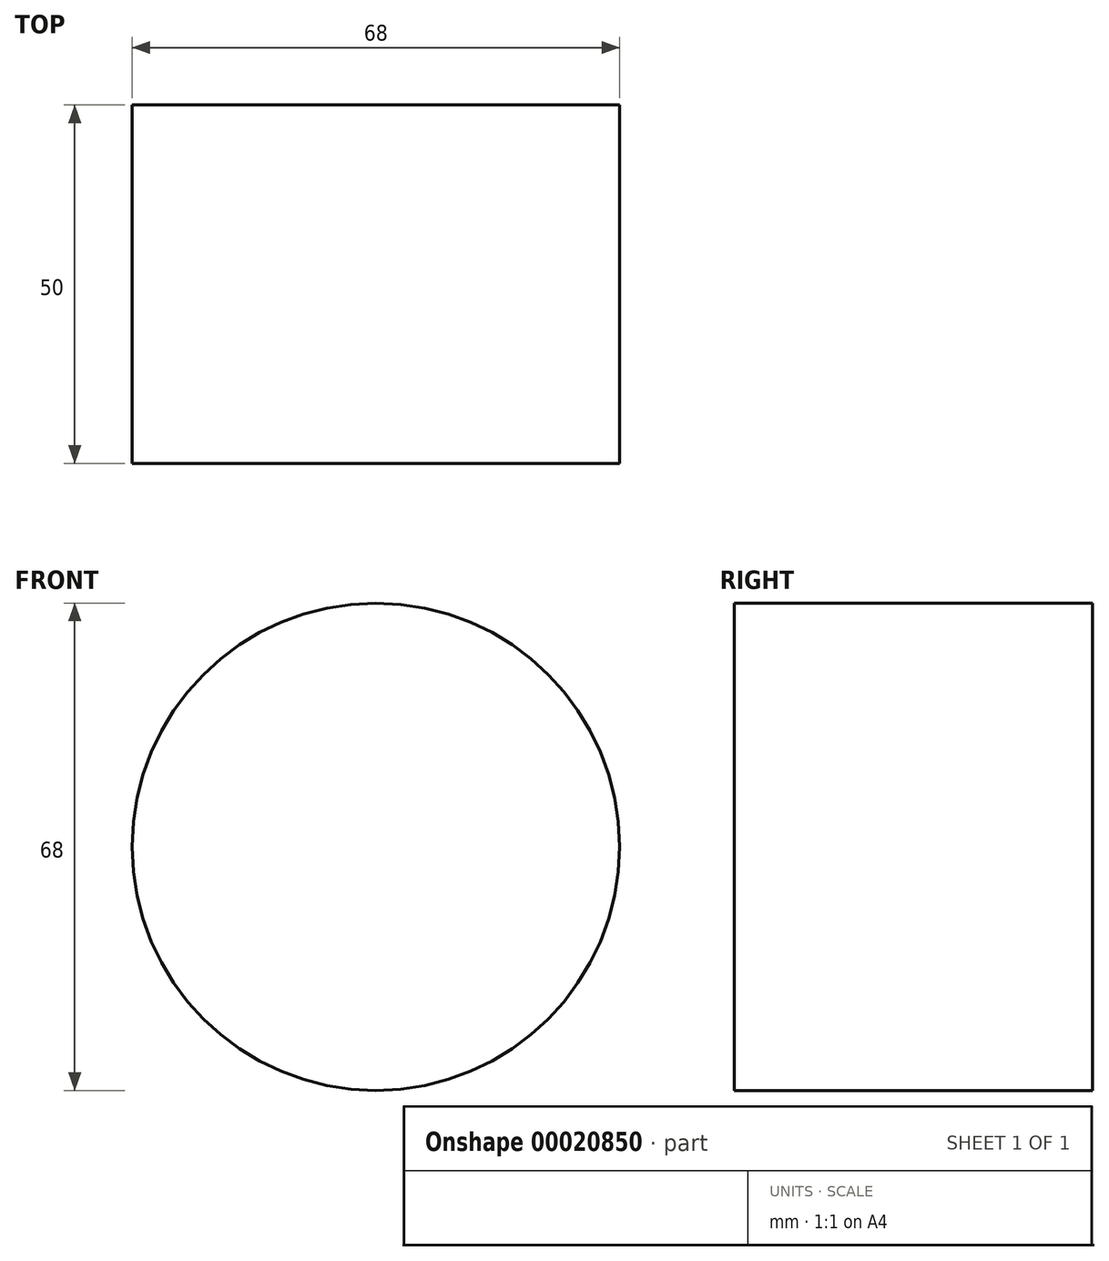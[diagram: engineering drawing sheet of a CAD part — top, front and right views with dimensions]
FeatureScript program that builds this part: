
annotation { "Feature Type Name" : "Feature", "Feature Type Description" : "" }
export const myFeature = defineFeature(function(context is Context, id is Id, definition is map)
    precondition{}
    {
        {
            var Q0;
            Q0=qCreatedBy(makeId("Front.planeOp"),FACE);
            var sketch = newSketch(context, id + "F0", { "sketchPlane" : qUnion([Q0])});
            skCircle(sketch, "E0", {"center": v(0, 0) * mm, "radius": 34 * mm});
            skSolve(sketch);
        }
        {
            var Q0;
            Q0=makeQuery(id+"F0.imprint","IMPRINT",FACE,{"disambiguationData":[TD([[makeQuery(id+"F0.imprint","IMPRINT",EDGE,{"derivedFrom":sQuery(id+"F0.wireOp",EDGE,"E0")}),1.0]])]});
            extrude(context, id + "F1", {"entities" : qUnion([Q0]), "depth" : 50 * mm});
        }
    });
